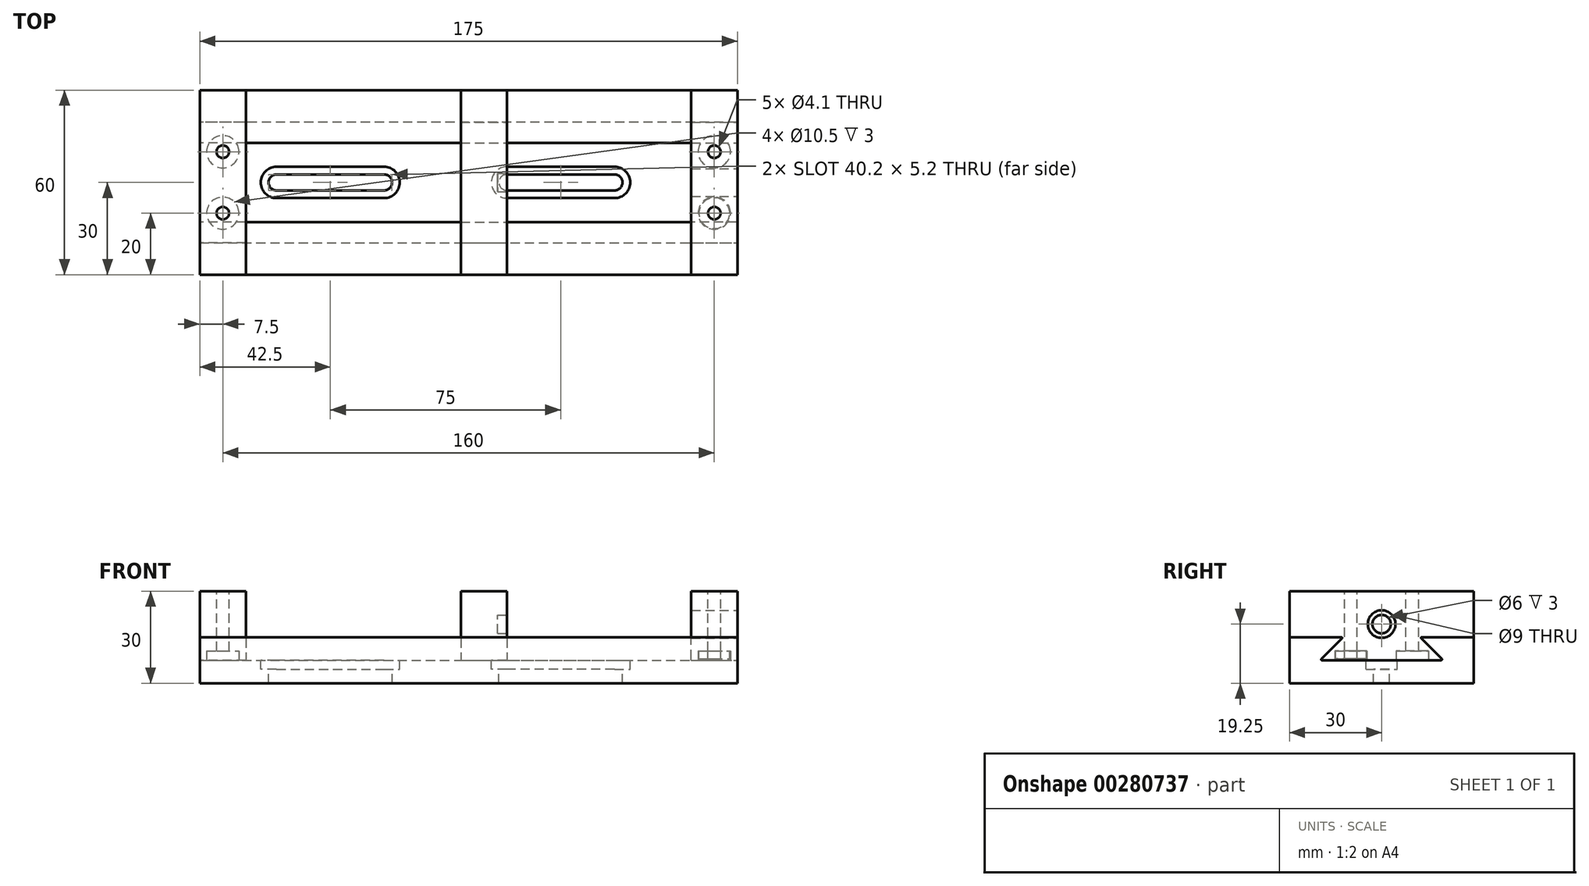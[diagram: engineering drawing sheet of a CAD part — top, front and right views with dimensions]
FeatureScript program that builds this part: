
annotation { "Feature Type Name" : "Feature", "Feature Type Description" : "" }
export const myFeature = defineFeature(function(context is Context, id is Id, definition is map)
    precondition{}
    {
        {
            var Q0;
            Q0=qCreatedBy(makeId("Top.planeOp"),FACE);
            var sketch = newSketch(context, id + "F0", { "sketchPlane" : qUnion([Q0])});
            skLineSegment(sketch, "E0.bottom", {"start": v(87.5, -30) * mm, "end": v(-87.5, -30) * mm});
            skLineSegment(sketch, "E0.top", {"start": v(87.5, 30) * mm, "end": v(-87.5, 30) * mm});
            skLineSegment(sketch, "E0.left", {"start": v(87.5, -30) * mm, "end": v(87.5, 30) * mm});
            skLineSegment(sketch, "E0.right", {"start": v(-87.5, -30) * mm, "end": v(-87.5, 30) * mm});
            skPoint(sketch, "E0.middle", {"position": v(0, 0) * mm});
            skSolve(sketch);
        }
        {
            var Q0;
            Q0=makeQuery(id+"F0.imprint","IMPRINT",FACE,{"disambiguationData":[TD([[makeQuery(id+"F0.imprint","IMPRINT",EDGE,{"derivedFrom":sQuery(id+"F0.wireOp",EDGE,"E0.bottom")}),-1.0]])]});
            extrude(context, id + "F1", {"entities" : qUnion([Q0]), "depth" : 15 * mm});
        }
        {
            var Q0;
            Q0=makeQuery(id+"F1.opExtrude","SWEPT_FACE",FACE,{"disambiguationData":[OSD([sQuery(id+"F0.wireOp",EDGE,"E0.left")])]});
            var sketch = newSketch(context, id + "F2", { "sketchPlane" : qUnion([Q0])});
            skLineSegment(sketch, "E1", {"start": v(-30, 7.5) * mm, "end": v(30, 7.5) * mm});
            skLineSegment(sketch, "E2", {"start": v(-20, 7.5) * mm, "end": v(-8.89, 18.61) * mm});
            skLineSegment(sketch, "E3", {"start": v(20, 7.5) * mm, "end": v(9.76, 17.74) * mm});
            skLineSegment(sketch, "E4", {"start": v(-8.89, 18.61) * mm, "end": v(9.76, 17.74) * mm});
            skSolve(sketch);
        }
        {
            var Q0;
            {var subQ0=sQuery(id+"F2.wireOp",EDGE,"E2");var subQ1=sQuery(id+"F2.wireOp",EDGE,"E1");var subQ2=makeQuery(id+"F2.imprint","INTERSECT",VERTEX,{"derivedFrom":[subQ1,subQ0]});Q0=makeQuery(id+"F2.imprint","IMPRINT",FACE,{"disambiguationData":[TD([[makeQuery(id+"F2.imprint","IMPRINT",EDGE,{"disambiguationData":[TD([[subQ2,-1.0]])],"derivedFrom":subQ1}),1.0]])]});}
            var Q1;
            {var subQ0=sQuery(id+"F2.wireOp",EDGE,"E4");Q1=makeQuery(id+"F2.imprint","IMPRINT",FACE,{"disambiguationData":[TD([[makeQuery(id+"F2.imprint","IMPRINT",EDGE,{"derivedFrom":subQ0}),-1.0]])]});}
            extrude(context, id + "F3", {"entities" : qUnion([Q0, Q1]), "operationType" : NewBodyOperationType.REMOVE, "endBound" : BoundingType.THROUGH_ALL, "oppositeDirection" : true, "depth" : 25 * mm});
        }
        {
            var Q0;
            Q0=makeQuery(id+"F3.boolean.opBoolean","COPY",EDGE,{"derivedFrom":makeQuery(id+"F3.opExtrude","SWEPT_EDGE",EDGE,{"disambiguationData":[OSD([sQuery(id+"F2.wireOp",EDGE,"E1"),sQuery(id+"F2.wireOp",EDGE,"E2")])]})});
            var Q1;
            Q1=makeQuery(id+"F3.boolean.opBoolean","COPY",EDGE,{"derivedFrom":makeQuery(id+"F3.opExtrude","SWEPT_EDGE",EDGE,{"disambiguationData":[OSD([sQuery(id+"F2.wireOp",EDGE,"E1"),sQuery(id+"F2.wireOp",EDGE,"E3")])]})});
            var Q2;
            Q2=makeQuery(id+"F3.boolean.opBoolean","INTERSECT",EDGE,{"derivedFrom":[makeQuery(id+"F1.opExtrude","CAP_FACE",FACE,{"disambiguationData":[OSD([sQuery(id+"F0.wireOp",EDGE,"E0.bottom"),sQuery(id+"F0.wireOp",EDGE,"E0.top"),sQuery(id+"F0.wireOp",EDGE,"E0.left"),sQuery(id+"F0.wireOp",EDGE,"E0.right")])],"isStart":false}),makeQuery(id+"F3.opExtrude","SWEPT_FACE",FACE,{"disambiguationData":[OSD([sQuery(id+"F2.wireOp",EDGE,"E3")])]})]});
            var Q3;
            Q3=makeQuery(id+"F3.boolean.opBoolean","INTERSECT",EDGE,{"derivedFrom":[makeQuery(id+"F1.opExtrude","CAP_FACE",FACE,{"disambiguationData":[OSD([sQuery(id+"F0.wireOp",EDGE,"E0.bottom"),sQuery(id+"F0.wireOp",EDGE,"E0.top"),sQuery(id+"F0.wireOp",EDGE,"E0.left"),sQuery(id+"F0.wireOp",EDGE,"E0.right")])],"isStart":false}),makeQuery(id+"F3.opExtrude","SWEPT_FACE",FACE,{"disambiguationData":[OSD([sQuery(id+"F2.wireOp",EDGE,"E2")])]})]});
            fillet(context, id + "F4", {"entities" : qUnion([Q0, Q1, Q2, Q3]), "radius" : .25 * mm, "tangentPropagation" : true, "allowEdgeOverflow" : false});
        }
        {
            var Q0;
            Q0=makeQuery(id+"F1.opExtrude","SWEPT_FACE",FACE,{"disambiguationData":[OSD([sQuery(id+"F0.wireOp",EDGE,"E0.left")])]});
            var sketch = newSketch(context, id + "F5", { "sketchPlane" : qUnion([Q0])});
            skLineSegment(sketch, "E5.0.0", {"start": v(30, 15) * mm, "end": v(13.1, 15) * mm});
            skArc(sketch, "E5.0.1", {"start": v(13.1, 15) * mm, "mid": v(12.87, 14.85) * mm, "end": v(12.93, 14.57) * mm});
            skLineSegment(sketch, "E5.0.2", {"start": v(12.93, 14.57) * mm, "end": v(19.57, 7.93) * mm});
            skArc(sketch, "E5.0.3", {"start": v(19.57, 7.93) * mm, "mid": v(19.63, 7.65) * mm, "end": v(19.4, 7.5) * mm});
            skLineSegment(sketch, "E5.0.4", {"start": v(19.4, 7.5) * mm, "end": v(-19.4, 7.5) * mm});
            skArc(sketch, "E5.0.5", {"start": v(-19.4, 7.5) * mm, "mid": v(-19.63, 7.65) * mm, "end": v(-19.57, 7.93) * mm});
            skLineSegment(sketch, "E5.0.6", {"start": v(-19.57, 7.93) * mm, "end": v(-12.93, 14.57) * mm});
            skArc(sketch, "E5.0.7", {"start": v(-12.93, 14.57) * mm, "mid": v(-12.87, 14.85) * mm, "end": v(-13.1, 15) * mm});
            skLineSegment(sketch, "E5.0.8", {"start": v(-13.1, 15) * mm, "end": v(-30, 15) * mm});
            skLineSegment(sketch, "E6.bottom", {"start": v(-30, 15) * mm, "end": v(-13.1, 15) * mm});
            skLineSegment(sketch, "E6.top", {"start": v(-30, 30) * mm, "end": v(30, 30) * mm});
            skLineSegment(sketch, "E6.left", {"start": v(-30, 15) * mm, "end": v(-30, 30) * mm});
            skLineSegment(sketch, "E6.right", {"start": v(30, 15) * mm, "end": v(30, 30) * mm});
            skLineSegment(sketch, "E7.trimOffspring", {"start": v(13.1, 15) * mm, "end": v(30, 15) * mm});
            skPoint(sketch, "E5.0.10.end.orphan", {"position": v(30, 0) * mm});
            skPoint(sketch, "E5.0.9.end.orphan", {"position": v(-30, 0) * mm});
            skSolve(sketch);
        }
        {
            var Q0;
            Q0=makeQuery(id+"F5.imprint","IMPRINT",FACE,{"disambiguationData":[TD([[makeQuery(id+"F5.imprint","IMPRINT",EDGE,{"derivedFrom":sQuery(id+"F5.wireOp",EDGE,"E5.0.1")}),-1.0]])]});
            extrude(context, id + "F6", {"entities" : qUnion([Q0]), "oppositeDirection" : true, "depth" : 15 * mm});
        }
        {
            var Q0;
            Q0=makeQuery(id+"F6.opExtrude","CAP_FACE",FACE,{"disambiguationData":[OSD([sQuery(id+"F5.wireOp",EDGE,"E5.0.1"),sQuery(id+"F5.wireOp",EDGE,"E5.0.2"),sQuery(id+"F5.wireOp",EDGE,"E5.0.3"),sQuery(id+"F5.wireOp",EDGE,"E5.0.4"),sQuery(id+"F5.wireOp",EDGE,"E5.0.5"),sQuery(id+"F5.wireOp",EDGE,"E5.0.6"),sQuery(id+"F5.wireOp",EDGE,"E5.0.7"),sQuery(id+"F5.wireOp",EDGE,"E6.bottom"),sQuery(id+"F5.wireOp",EDGE,"E6.top"),sQuery(id+"F5.wireOp",EDGE,"E6.left"),sQuery(id+"F5.wireOp",EDGE,"E6.right"),sQuery(id+"F5.wireOp",EDGE,"E7.trimOffspring")])],"isStart":true});
            var sketch = newSketch(context, id + "F7", { "sketchPlane" : qUnion([Q0])});
            skCircle(sketch, "E8", {"center": v(0, 19.25) * mm, "radius": 4.5 * mm});
            skLineSegment(sketch, "E9", {"start": v(0, 7.5) * mm, "end": v(0, 30) * mm, "construction": true});
            skSolve(sketch);
        }
        {
            var Q0;
            Q0=makeQuery(id+"F7.imprint","IMPRINT",FACE,{"disambiguationData":[TD([[makeQuery(id+"F7.imprint","IMPRINT",EDGE,{"derivedFrom":sQuery(id+"F7.wireOp",EDGE,"E8")}),1.0]])]});
            extrude(context, id + "F8", {"entities" : qUnion([Q0]), "operationType" : NewBodyOperationType.REMOVE, "endBound" : BoundingType.THROUGH_ALL, "oppositeDirection" : true, "depth" : 25 * mm});
        }
        {
            var Q0;
            Q0=makeQuery(id+"F1.opExtrude","SWEPT_FACE",FACE,{"disambiguationData":[OSD([sQuery(id+"F0.wireOp",EDGE,"E0.right")])]});
            var sketch = newSketch(context, id + "F9", { "sketchPlane" : qUnion([Q0])});
            skLineSegment(sketch, "E10.0.0", {"start": v(-19.57, 7.93) * mm, "end": v(-12.93, 14.57) * mm});
            skArc(sketch, "E10.0.1", {"start": v(-12.93, 14.57) * mm, "mid": v(-12.87, 14.85) * mm, "end": v(-13.1, 15) * mm});
            skLineSegment(sketch, "E10.0.2", {"start": v(-13.1, 15) * mm, "end": v(-30, 15) * mm});
            skLineSegment(sketch, "E10.0.6", {"start": v(30, 15) * mm, "end": v(13.1, 15) * mm});
            skArc(sketch, "E10.0.7", {"start": v(13.1, 15) * mm, "mid": v(12.87, 14.85) * mm, "end": v(12.93, 14.57) * mm});
            skLineSegment(sketch, "E10.0.8", {"start": v(12.93, 14.57) * mm, "end": v(19.57, 7.93) * mm});
            skArc(sketch, "E10.0.9", {"start": v(19.57, 7.93) * mm, "mid": v(19.63, 7.65) * mm, "end": v(19.4, 7.5) * mm});
            skLineSegment(sketch, "E10.0.10", {"start": v(19.4, 7.5) * mm, "end": v(-19.4, 7.5) * mm});
            skArc(sketch, "E10.0.11", {"start": v(-19.4, 7.5) * mm, "mid": v(-19.63, 7.65) * mm, "end": v(-19.57, 7.93) * mm});
            skLineSegment(sketch, "E11.bottom", {"start": v(-30, 15) * mm, "end": v(-13.1, 15) * mm});
            skLineSegment(sketch, "E11.top", {"start": v(-30, 30) * mm, "end": v(30, 30) * mm});
            skLineSegment(sketch, "E11.left", {"start": v(-30, 15) * mm, "end": v(-30, 30) * mm});
            skLineSegment(sketch, "E11.right", {"start": v(30, 15) * mm, "end": v(30, 30) * mm});
            skLineSegment(sketch, "E12.trimOffspring", {"start": v(13.1, 15) * mm, "end": v(30, 15) * mm});
            skPoint(sketch, "E10.0.4.end.orphan", {"position": v(30, 0) * mm});
            skPoint(sketch, "E10.0.3.end.orphan", {"position": v(-30, 0) * mm});
            skSolve(sketch);
        }
        {
            var Q0;
            Q0=makeQuery(id+"F9.imprint","IMPRINT",FACE,{"disambiguationData":[TD([[makeQuery(id+"F9.imprint","IMPRINT",EDGE,{"derivedFrom":sQuery(id+"F9.wireOp",EDGE,"E10.0.0")}),1.0]])]});
            extrude(context, id + "F10", {"entities" : qUnion([Q0]), "oppositeDirection" : true, "depth" : 15 * mm});
        }
        {
            var Q0;
            Q0=makeQuery(id+"F1.opExtrude","SWEPT_FACE",FACE,{"disambiguationData":[OSD([sQuery(id+"F0.wireOp",EDGE,"E0.right")])]});
            cPlane(context, id + "F11", {"entities" : qUnion([Q0]), "cplaneType" : CPlaneType.OFFSET, "offset" : 100 * mm, "oppositeDirection" : true, "width" : 150 * mm, "height" : 150 * mm});
        }
        {
            var Q0;
            Q0=qCreatedBy(id+"F11.planeOp",FACE);
            var sketch = newSketch(context, id + "F12", { "sketchPlane" : qUnion([Q0])});
            skLineSegment(sketch, "E13.0.0", {"start": v(-19.57, 7.93) * mm, "end": v(-12.93, 14.57) * mm});
            skArc(sketch, "E13.0.1", {"start": v(-12.93, 14.57) * mm, "mid": v(-12.87, 14.85) * mm, "end": v(-13.1, 15) * mm});
            skLineSegment(sketch, "E13.0.2", {"start": v(-13.1, 15) * mm, "end": v(-30, 15) * mm});
            skLineSegment(sketch, "E13.0.6", {"start": v(30, 15) * mm, "end": v(13.1, 15) * mm});
            skArc(sketch, "E13.0.7", {"start": v(13.1, 15) * mm, "mid": v(12.87, 14.85) * mm, "end": v(12.93, 14.57) * mm});
            skLineSegment(sketch, "E13.0.8", {"start": v(12.93, 14.57) * mm, "end": v(19.57, 7.93) * mm});
            skArc(sketch, "E13.0.9", {"start": v(19.57, 7.93) * mm, "mid": v(19.63, 7.65) * mm, "end": v(19.4, 7.5) * mm});
            skLineSegment(sketch, "E13.0.10", {"start": v(19.4, 7.5) * mm, "end": v(-19.4, 7.5) * mm});
            skArc(sketch, "E13.0.11", {"start": v(-19.4, 7.5) * mm, "mid": v(-19.63, 7.65) * mm, "end": v(-19.57, 7.93) * mm});
            skLineSegment(sketch, "E14.bottom", {"start": v(-30, 15) * mm, "end": v(-13.1, 15) * mm});
            skLineSegment(sketch, "E14.top", {"start": v(-30, 30) * mm, "end": v(30, 30) * mm});
            skLineSegment(sketch, "E14.left", {"start": v(-30, 15) * mm, "end": v(-30, 30) * mm});
            skLineSegment(sketch, "E14.right", {"start": v(30, 15) * mm, "end": v(30, 30) * mm});
            skLineSegment(sketch, "E15.trimOffspring", {"start": v(13.1, 15) * mm, "end": v(30, 15) * mm});
            skPoint(sketch, "E13.0.4.end.orphan", {"position": v(30, 0) * mm});
            skPoint(sketch, "E13.0.3.end.orphan", {"position": v(-30, 0) * mm});
            skSolve(sketch);
        }
        {
            var Q0;
            Q0=makeQuery(id+"F12.imprint","IMPRINT",FACE,{"disambiguationData":[TD([[makeQuery(id+"F12.imprint","IMPRINT",EDGE,{"derivedFrom":sQuery(id+"F12.wireOp",EDGE,"E13.0.0")}),-1.0]])]});
            extrude(context, id + "F13", {"entities" : qUnion([Q0]), "depth" : 15 * mm});
        }
        {
            var Q0;
            Q0=makeQuery(id+"F13.opExtrude","CAP_FACE",FACE,{"disambiguationData":[OSD([sQuery(id+"F12.wireOp",EDGE,"E13.0.0"),sQuery(id+"F12.wireOp",EDGE,"E13.0.1"),sQuery(id+"F12.wireOp",EDGE,"E13.0.7"),sQuery(id+"F12.wireOp",EDGE,"E13.0.8"),sQuery(id+"F12.wireOp",EDGE,"E13.0.9"),sQuery(id+"F12.wireOp",EDGE,"E13.0.10"),sQuery(id+"F12.wireOp",EDGE,"E13.0.11"),sQuery(id+"F12.wireOp",EDGE,"E14.bottom"),sQuery(id+"F12.wireOp",EDGE,"E14.top"),sQuery(id+"F12.wireOp",EDGE,"E14.left"),sQuery(id+"F12.wireOp",EDGE,"E14.right"),sQuery(id+"F12.wireOp",EDGE,"E15.trimOffspring")])],"isStart":true});
            var sketch = newSketch(context, id + "F14", { "sketchPlane" : qUnion([Q0])});
            skCircle(sketch, "E16", {"center": v(0, 19.25) * mm, "radius": 3 * mm});
            skSolve(sketch);
        }
        {
            var Q0;
            Q0=makeQuery(id+"F14.imprint","IMPRINT",FACE,{"disambiguationData":[TD([[makeQuery(id+"F14.imprint","IMPRINT",EDGE,{"derivedFrom":sQuery(id+"F14.wireOp",EDGE,"E16")}),1.0]])]});
            extrude(context, id + "F15", {"entities" : qUnion([Q0]), "operationType" : NewBodyOperationType.REMOVE, "oppositeDirection" : true, "depth" : 3 * mm});
        }
        {
            var Q0;
            Q0=makeQuery(id+"F6.opExtrude","SWEPT_FACE",FACE,{"disambiguationData":[OSD([sQuery(id+"F5.wireOp",EDGE,"E6.top")])]});
            var sketch = newSketch(context, id + "F16", { "sketchPlane" : qUnion([Q0])});
            skLineSegment(sketch, "E17", {"start": v(80, 30) * mm, "end": v(80, -30) * mm, "construction": true});
            skCircle(sketch, "E18", {"center": v(80, 10) * mm, "radius": 2.05 * mm});
            skCircle(sketch, "E19", {"center": v(80, -10) * mm, "radius": 2.05 * mm});
            skLineSegment(sketch, "E20", {"start": v(72.5, 0) * mm, "end": v(87.5, 0) * mm, "construction": true});
            skSolve(sketch);
        }
        {
            var Q0;
            Q0=makeQuery(id+"F16.imprint","IMPRINT",FACE,{"disambiguationData":[TD([[makeQuery(id+"F16.imprint","IMPRINT",EDGE,{"derivedFrom":sQuery(id+"F16.wireOp",EDGE,"E18")}),1.0]])]});
            var Q1;
            Q1=makeQuery(id+"F16.imprint","IMPRINT",FACE,{"disambiguationData":[TD([[makeQuery(id+"F16.imprint","IMPRINT",EDGE,{"derivedFrom":sQuery(id+"F16.wireOp",EDGE,"E19")}),1.0]])]});
            var Q2;
            Q2=makeQuery(id+"F3.boolean.opBoolean","COPY",FACE,{"derivedFrom":makeQuery(id+"F3.opExtrude","SWEPT_FACE",FACE,{"disambiguationData":[OSD([sQuery(id+"F2.wireOp",EDGE,"E1")])]})});
            extrude(context, id + "F17", {"entities" : qUnion([Q0, Q1]), "operationType" : NewBodyOperationType.REMOVE, "endBound" : BoundingType.UP_TO_SURFACE, "oppositeDirection" : true, "endBoundEntityFace" : qUnion([Q2]), "depth" : 25 * mm});
        }
        {
            var Q0;
            Q0=makeQuery(id+"F10.opExtrude","SWEPT_FACE",FACE,{"disambiguationData":[OSD([sQuery(id+"F9.wireOp",EDGE,"E11.top")])]});
            var sketch = newSketch(context, id + "F18", { "sketchPlane" : qUnion([Q0])});
            skLineSegment(sketch, "E21", {"start": v(-80, 30) * mm, "end": v(-80, -30) * mm, "construction": true});
            skLineSegment(sketch, "E22", {"start": v(-72.5, 0) * mm, "end": v(-87.5, 0) * mm, "construction": true});
            skCircle(sketch, "E23", {"center": v(-80, 10) * mm, "radius": 2.05 * mm});
            skCircle(sketch, "E24", {"center": v(-80, -10) * mm, "radius": 2.05 * mm});
            skSolve(sketch);
        }
        {
            var Q0;
            Q0=makeQuery(id+"F18.imprint","IMPRINT",FACE,{"disambiguationData":[TD([[makeQuery(id+"F18.imprint","IMPRINT",EDGE,{"derivedFrom":sQuery(id+"F18.wireOp",EDGE,"E23")}),1.0]])]});
            var Q1;
            Q1=makeQuery(id+"F18.imprint","IMPRINT",FACE,{"disambiguationData":[TD([[makeQuery(id+"F18.imprint","IMPRINT",EDGE,{"derivedFrom":sQuery(id+"F18.wireOp",EDGE,"E24")}),1.0]])]});
            var Q2;
            Q2=makeQuery(id+"F3.boolean.opBoolean","COPY",FACE,{"derivedFrom":makeQuery(id+"F3.opExtrude","SWEPT_FACE",FACE,{"disambiguationData":[OSD([sQuery(id+"F2.wireOp",EDGE,"E1")])]})});
            extrude(context, id + "F19", {"entities" : qUnion([Q0, Q1]), "operationType" : NewBodyOperationType.REMOVE, "endBound" : BoundingType.UP_TO_SURFACE, "oppositeDirection" : true, "endBoundEntityFace" : qUnion([Q2]), "depth" : 25 * mm});
        }
        {
            var Q0;
            Q0=makeQuery(id+"F10.opExtrude","SWEPT_FACE",FACE,{"disambiguationData":[OSD([sQuery(id+"F9.wireOp",EDGE,"E10.0.10")])]});
            var sketch = newSketch(context, id + "F20", { "sketchPlane" : qUnion([Q0])});
            skCircle(sketch, "E25", {"center": v(-80, 10) * mm, "radius": 5.25 * mm});
            skCircle(sketch, "E26", {"center": v(-80, -10) * mm, "radius": 5.25 * mm});
            skSolve(sketch);
        }
        {
            var Q0;
            Q0=makeQuery(id+"F20.imprint","IMPRINT",FACE,{"disambiguationData":[TD([[makeQuery(id+"F20.imprint","IMPRINT",EDGE,{"derivedFrom":sQuery(id+"F20.wireOp",EDGE,"E25")}),1.0]])]});
            var Q1;
            Q1=makeQuery(id+"F20.imprint","IMPRINT",FACE,{"disambiguationData":[TD([[makeQuery(id+"F20.imprint","IMPRINT",EDGE,{"derivedFrom":sQuery(id+"F20.wireOp",EDGE,"E26")}),1.0]])]});
            extrude(context, id + "F21", {"entities" : qUnion([Q0, Q1]), "operationType" : NewBodyOperationType.REMOVE, "oppositeDirection" : true, "depth" : 3 * mm});
        }
        {
            var Q0;
            Q0=makeQuery(id+"F6.opExtrude","SWEPT_FACE",FACE,{"disambiguationData":[OSD([sQuery(id+"F5.wireOp",EDGE,"E5.0.4")])]});
            var sketch = newSketch(context, id + "F22", { "sketchPlane" : qUnion([Q0])});
            skCircle(sketch, "E27", {"center": v(80, 10) * mm, "radius": 5.25 * mm});
            skCircle(sketch, "E28", {"center": v(80, -10) * mm, "radius": 5.25 * mm});
            skSolve(sketch);
        }
        {
            var Q0;
            Q0=makeQuery(id+"F22.imprint","IMPRINT",FACE,{"disambiguationData":[TD([[makeQuery(id+"F22.imprint","IMPRINT",EDGE,{"derivedFrom":sQuery(id+"F22.wireOp",EDGE,"E27")}),1.0]])]});
            var Q1;
            Q1=makeQuery(id+"F22.imprint","IMPRINT",FACE,{"disambiguationData":[TD([[makeQuery(id+"F22.imprint","IMPRINT",EDGE,{"derivedFrom":sQuery(id+"F22.wireOp",EDGE,"E28")}),1.0]])]});
            extrude(context, id + "F23", {"entities" : qUnion([Q0, Q1]), "operationType" : NewBodyOperationType.REMOVE, "oppositeDirection" : true, "depth" : 3 * mm});
        }
        {
            var Q0;
            Q0=makeQuery(id+"F23.boolean.opBoolean","COPY",FACE,{"derivedFrom":makeQuery(id+"F23.opExtrude","CAP_FACE",FACE,{"disambiguationData":[OSD([sQuery(id+"F2.wireOp",EDGE,"E1"),sQuery(id+"F16.wireOp",EDGE,"E19"),sQuery(id+"F22.wireOp",EDGE,"E27")])],"isStart":false})});
            var sketch = newSketch(context, id + "F24", { "sketchPlane" : qUnion([Q0])});
            skCircle(sketch, "E29", {"center": v(80, 10) * mm, "radius": 5 * mm});
            skSolve(sketch);
        }
        {
            var Q0;
            Q0=makeQuery(id+"F24.imprint","IMPRINT",FACE,{"disambiguationData":[TD([[makeQuery(id+"F24.imprint","IMPRINT",EDGE,{"derivedFrom":sQuery(id+"F24.wireOp",EDGE,"E29")}),1.0]])]});
            var Q1;
            Q1=makeQuery(id+"F24.imprint","IMPRINT",FACE,{"disambiguationData":[TD([[makeQuery(id+"F24.imprint","IMPRINT",EDGE,{"derivedFrom":makeQuery(id+"F23.boolean.opBoolean","COPY",EDGE,{"derivedFrom":makeQuery(id+"F23.opExtrude","CAP_EDGE",EDGE,{"disambiguationData":[OSD([sQuery(id+"F2.wireOp",EDGE,"E1"),sQuery(id+"F16.wireOp",EDGE,"E19")])],"isStart":false})})}),-1.0]])]});
            extrude(context, id + "F25", {"entities" : qUnion([Q0, Q1]), "depth" : 2.5 * mm});
        }
        {
            var Q0;
            Q0=makeQuery(id+"F3.boolean.opBoolean","COPY",FACE,{"derivedFrom":makeQuery(id+"F3.opExtrude","SWEPT_FACE",FACE,{"disambiguationData":[OSD([sQuery(id+"F2.wireOp",EDGE,"E1")])]})});
            var sketch = newSketch(context, id + "F26", { "sketchPlane" : qUnion([Q0])});
            skLineSegment(sketch, "E30", {"start": v(12.5, 0) * mm, "end": v(47.5, 0) * mm});
            skLineSegment(sketch, "E31", {"start": v(-27.5, 0) * mm, "end": v(-62.5, 0) * mm});
            skArc(sketch, "E32.0.startCap", {"start": v(-27.5, 2.6) * mm, "mid": v(-24.9, 0) * mm, "end": v(-27.5, -2.6) * mm});
            skArc(sketch, "E32.0.endCap", {"start": v(-62.5, -2.6) * mm, "mid": v(-65.1, 0) * mm, "end": v(-62.5, 2.6) * mm});
            skLineSegment(sketch, "E32.0.left", {"start": v(-27.5, -2.6) * mm, "end": v(-62.5, -2.6) * mm});
            skLineSegment(sketch, "E32.0.right", {"start": v(-27.5, 2.6) * mm, "end": v(-62.5, 2.6) * mm});
            skArc(sketch, "E32.1.startCap", {"start": v(12.5, -2.6) * mm, "mid": v(9.9, 0) * mm, "end": v(12.5, 2.6) * mm});
            skArc(sketch, "E32.1.endCap", {"start": v(47.5, 2.6) * mm, "mid": v(50.1, 0) * mm, "end": v(47.5, -2.6) * mm});
            skLineSegment(sketch, "E32.1.left", {"start": v(12.5, 2.6) * mm, "end": v(47.5, 2.6) * mm});
            skLineSegment(sketch, "E32.1.right", {"start": v(12.5, -2.6) * mm, "end": v(47.5, -2.6) * mm});
            skSolve(sketch);
        }
        {
            var Q0;
            Q0 = qSketchRegion(id + "F26", true);
            extrude(context, id + "F27", {"entities" : qUnion([Q0]), "operationType" : NewBodyOperationType.REMOVE, "oppositeDirection" : true, "depth" : 25 * mm});
        }
        {
            var Q0;
            Q0=makeQuery(id+"F3.boolean.opBoolean","COPY",FACE,{"derivedFrom":makeQuery(id+"F3.opExtrude","SWEPT_FACE",FACE,{"disambiguationData":[OSD([sQuery(id+"F2.wireOp",EDGE,"E1")])]})});
            var sketch = newSketch(context, id + "F28", { "sketchPlane" : qUnion([Q0])});
            skLineSegment(sketch, "E33", {"start": v(-27.5, 0) * mm, "end": v(-62.5, 0) * mm});
            skLineSegment(sketch, "E34", {"start": v(12.5, 0) * mm, "end": v(47.5, 0) * mm});
            skArc(sketch, "E35.0.startCap", {"start": v(12.5, -5.1) * mm, "mid": v(7.4, 0) * mm, "end": v(12.5, 5.1) * mm});
            skArc(sketch, "E35.0.endCap", {"start": v(47.5, 5.1) * mm, "mid": v(52.6, 0) * mm, "end": v(47.5, -5.1) * mm});
            skLineSegment(sketch, "E35.0.left", {"start": v(12.5, 5.1) * mm, "end": v(47.5, 5.1) * mm});
            skLineSegment(sketch, "E35.0.right", {"start": v(12.5, -5.1) * mm, "end": v(47.5, -5.1) * mm});
            skArc(sketch, "E35.1.startCap", {"start": v(-27.5, 5.1) * mm, "mid": v(-22.4, 0) * mm, "end": v(-27.5, -5.1) * mm});
            skArc(sketch, "E35.1.endCap", {"start": v(-62.5, -5.1) * mm, "mid": v(-67.6, 0) * mm, "end": v(-62.5, 5.1) * mm});
            skLineSegment(sketch, "E35.1.left", {"start": v(-27.5, -5.1) * mm, "end": v(-62.5, -5.1) * mm});
            skLineSegment(sketch, "E35.1.right", {"start": v(-27.5, 5.1) * mm, "end": v(-62.5, 5.1) * mm});
            skSolve(sketch);
        }
        {
            var Q0;
            Q0 = qSketchRegion(id + "F28", true);
            extrude(context, id + "F29", {"entities" : qUnion([Q0]), "operationType" : NewBodyOperationType.REMOVE, "oppositeDirection" : true, "depth" : 3 * mm});
        }
    });
